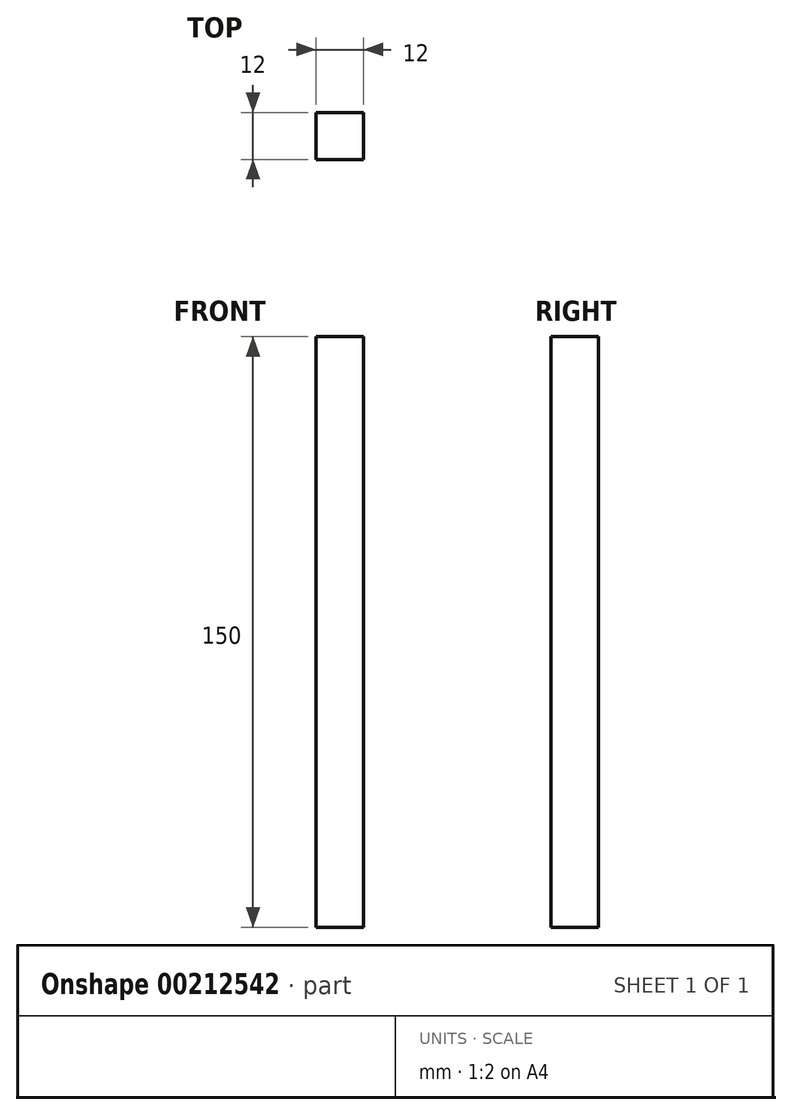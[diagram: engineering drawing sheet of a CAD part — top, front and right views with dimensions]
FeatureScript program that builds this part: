
annotation { "Feature Type Name" : "Feature", "Feature Type Description" : "" }
export const myFeature = defineFeature(function(context is Context, id is Id, definition is map)
    precondition{}
    {
        {
            var Q0;
            Q0=qCreatedBy(makeId("Top.planeOp"),FACE);
            var sketch = newSketch(context, id + "F0", { "sketchPlane" : qUnion([Q0])});
            skLineSegment(sketch, "E0.bottom", {"start": v(6, 6) * mm, "end": v(-6, 6) * mm});
            skLineSegment(sketch, "E0.top", {"start": v(6, -6) * mm, "end": v(-6, -6) * mm});
            skLineSegment(sketch, "E0.left", {"start": v(6, 6) * mm, "end": v(6, -6) * mm});
            skLineSegment(sketch, "E0.right", {"start": v(-6, 6) * mm, "end": v(-6, -6) * mm});
            skPoint(sketch, "E0.middle", {"position": v(0, 0) * mm});
            skSolve(sketch);
        }
        {
            var Q0;
            Q0=makeQuery(id+"F0.imprint","IMPRINT",FACE,{"disambiguationData":[TD([[makeQuery(id+"F0.imprint","IMPRINT",EDGE,{"derivedFrom":sQuery(id+"F0.wireOp",EDGE,"E0.bottom")}),1.0]])]});
            extrude(context, id + "F1", {"entities" : qUnion([Q0]), "depth" : 150 * mm});
        }
    });
